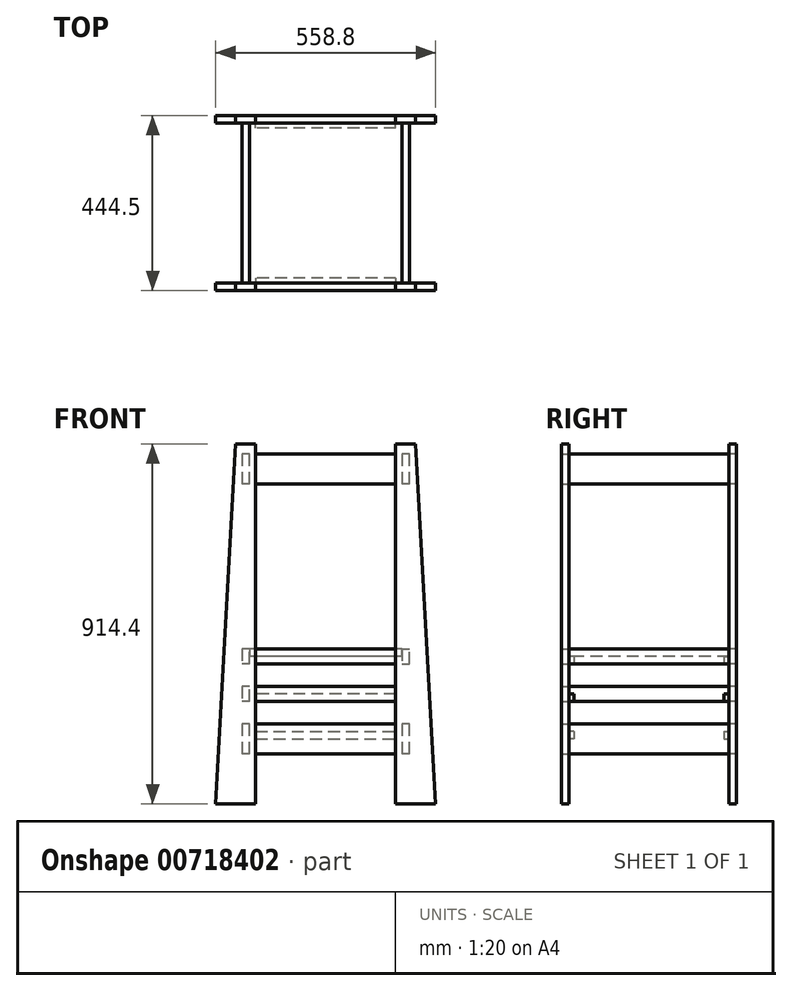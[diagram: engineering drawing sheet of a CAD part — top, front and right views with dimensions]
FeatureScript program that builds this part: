
annotation { "Feature Type Name" : "Feature", "Feature Type Description" : "" }
export const myFeature = defineFeature(function(context is Context, id is Id, definition is map)
    precondition{}
    {
        {
            var Q0;
            Q0=qCreatedBy(makeId("Front.planeOp"),FACE);
            var sketch = newSketch(context, id + "F0", { "sketchPlane" : qUnion([Q0])});
            skLineSegment(sketch, "E0", {"start": v(-279.4, 0) * mm, "end": v(-228.6, 914.4) * mm});
            skLineSegment(sketch, "E1", {"start": v(-228.6, 914.4) * mm, "end": v(-177.8, 914.4) * mm});
            skLineSegment(sketch, "E2", {"start": v(0, 494.04) * mm, "end": v(0, 0) * mm, "construction": true});
            skLineSegment(sketch, "E3", {"start": v(-279.4, 0) * mm, "end": v(-177.8, 0) * mm});
            skLineSegment(sketch, "E4", {"start": v(-177.8, 914.4) * mm, "end": v(-177.8, 0) * mm});
            skLineSegment(sketch, "E5.MirrorCS", {"start": v(228.6, 914.4) * mm, "end": v(177.8, 914.4) * mm});
            skLineSegment(sketch, "E6.MirrorCS", {"start": v(279.4, 0) * mm, "end": v(177.8, 0) * mm});
            skLineSegment(sketch, "E7.MirrorCS", {"start": v(177.8, 914.4) * mm, "end": v(177.8, 0) * mm});
            skLineSegment(sketch, "E8.bottom", {"start": v(-177.8, 889) * mm, "end": v(177.8, 889) * mm});
            skLineSegment(sketch, "E8.top", {"start": v(-177.8, 812.8) * mm, "end": v(177.8, 812.8) * mm});
            skLineSegment(sketch, "E8.left", {"start": v(-177.8, 889) * mm, "end": v(-177.8, 812.8) * mm});
            skLineSegment(sketch, "E8.right", {"start": v(177.8, 889) * mm, "end": v(177.8, 812.8) * mm});
            skLineSegment(sketch, "E9.bottom", {"start": v(-177.8, 393.7) * mm, "end": v(177.8, 393.7) * mm});
            skLineSegment(sketch, "E9.top", {"start": v(-177.8, 355.6) * mm, "end": v(177.8, 355.6) * mm});
            skLineSegment(sketch, "E9.left", {"start": v(-177.8, 393.7) * mm, "end": v(-177.8, 355.6) * mm});
            skLineSegment(sketch, "E9.right", {"start": v(177.8, 393.7) * mm, "end": v(177.8, 355.6) * mm});
            skLineSegment(sketch, "E10.bottom", {"start": v(-177.8, 298.45) * mm, "end": v(177.8, 298.45) * mm});
            skLineSegment(sketch, "E10.top", {"start": v(-177.8, 260.35) * mm, "end": v(177.8, 260.35) * mm});
            skLineSegment(sketch, "E10.left", {"start": v(-177.8, 298.45) * mm, "end": v(-177.8, 260.35) * mm});
            skLineSegment(sketch, "E10.right", {"start": v(177.8, 298.45) * mm, "end": v(177.8, 260.35) * mm});
            skLineSegment(sketch, "E11.bottom", {"start": v(-177.8, 203.2) * mm, "end": v(177.8, 203.2) * mm});
            skLineSegment(sketch, "E11.top", {"start": v(-177.8, 127) * mm, "end": v(177.8, 127) * mm});
            skLineSegment(sketch, "E11.left", {"start": v(-177.8, 203.2) * mm, "end": v(-177.8, 127) * mm});
            skLineSegment(sketch, "E11.right", {"start": v(177.8, 203.2) * mm, "end": v(177.8, 127) * mm});
            skLineSegment(sketch, "E12", {"start": v(228.6, 914.4) * mm, "end": v(279.4, 0) * mm});
            skSolve(sketch);
        }
        {
            var Q0;
            Q0=makeQuery(id+"F0.imprint","IMPRINT",FACE,{"disambiguationData":[TD([[makeQuery(id+"F0.imprint","IMPRINT",EDGE,{"derivedFrom":sQuery(id+"F0.wireOp",EDGE,"E0")}),-1.0]])]});
            var Q1;
            {var subQ6=sQuery(id+"F0.wireOp",EDGE,"E5.MirrorCS");Q1=makeQuery(id+"F0.imprint","IMPRINT",FACE,{"disambiguationData":[TD([[makeQuery(id+"F0.imprint","IMPRINT",EDGE,{"derivedFrom":subQ6}),1.0]])]});}
            extrude(context, id + "F1", {"entities" : qUnion([Q0, Q1]), "depth" : 19.05 * mm, "offsetDistance" : 25.4 * mm});
        }
        {
            var Q0;
            Q0=makeQuery(id+"F0.imprint","IMPRINT",FACE,{"disambiguationData":[TD([[makeQuery(id+"F0.imprint","IMPRINT",EDGE,{"derivedFrom":sQuery(id+"F0.wireOp",EDGE,"E8.bottom")}),-1.0]])]});
            var Q1;
            Q1=makeQuery(id+"F0.imprint","IMPRINT",FACE,{"disambiguationData":[TD([[makeQuery(id+"F0.imprint","IMPRINT",EDGE,{"derivedFrom":sQuery(id+"F0.wireOp",EDGE,"E9.bottom")}),-1.0]])]});
            var Q2;
            Q2=makeQuery(id+"F0.imprint","IMPRINT",FACE,{"disambiguationData":[TD([[makeQuery(id+"F0.imprint","IMPRINT",EDGE,{"derivedFrom":sQuery(id+"F0.wireOp",EDGE,"E10.bottom")}),-1.0]])]});
            var Q3;
            Q3=makeQuery(id+"F0.imprint","IMPRINT",FACE,{"disambiguationData":[TD([[makeQuery(id+"F0.imprint","IMPRINT",EDGE,{"derivedFrom":sQuery(id+"F0.wireOp",EDGE,"E11.bottom")}),-1.0]])]});
            extrude(context, id + "F2", {"entities" : qUnion([Q0, Q1, Q2, Q3]), "depth" : 19.05 * mm, "offsetDistance" : 25.4 * mm});
        }
        {
            var Q0;
            Q0=qCreatedBy(makeId("Front.planeOp"),FACE);
            var sketch = newSketch(context, id + "F3", { "sketchPlane" : qUnion([Q0])});
            skLineSegment(sketch, "E13.0.0", {"start": v(177.8, 374.65) * mm, "end": v(0, 374.65) * mm});
            skLineSegment(sketch, "E13.0.2", {"start": v(0, 355.6) * mm, "end": v(177.8, 355.6) * mm});
            skLineSegment(sketch, "E13.1.0", {"start": v(177.8, 279.4) * mm, "end": v(0, 279.4) * mm});
            skLineSegment(sketch, "E13.1.2", {"start": v(0, 260.35) * mm, "end": v(177.8, 260.35) * mm});
            skLineSegment(sketch, "E13.2.2", {"start": v(177.8, 184.15) * mm, "end": v(0, 184.15) * mm});
            skLineSegment(sketch, "E14", {"start": v(177.8, 374.65) * mm, "end": v(177.8, 374.65) * mm});
            skLineSegment(sketch, "E15", {"start": v(177.8, 374.65) * mm, "end": v(177.8, 355.6) * mm});
            skLineSegment(sketch, "E16", {"start": v(177.8, 355.6) * mm, "end": v(177.8, 355.6) * mm});
            skLineSegment(sketch, "E17", {"start": v(177.8, 279.4) * mm, "end": v(177.8, 279.4) * mm});
            skLineSegment(sketch, "E18", {"start": v(177.8, 279.4) * mm, "end": v(177.8, 260.35) * mm});
            skLineSegment(sketch, "E19", {"start": v(177.8, 260.35) * mm, "end": v(177.8, 260.35) * mm});
            skLineSegment(sketch, "E20", {"start": v(177.8, 184.15) * mm, "end": v(177.8, 184.15) * mm});
            skLineSegment(sketch, "E21", {"start": v(177.8, 184.15) * mm, "end": v(177.8, 165.1) * mm});
            skLineSegment(sketch, "E22.0", {"start": v(0, 494.04) * mm, "end": v(0, 0) * mm, "construction": true});
            skPoint(sketch, "E13.0.1.end.orphan", {"position": v(-177.8, 355.6) * mm});
            skPoint(sketch, "E13.0.1.start.orphan", {"position": v(-177.8, 393.7) * mm});
            skPoint(sketch, "E23.orphan", {"position": v(-177.8, 260.35) * mm});
            skPoint(sketch, "E13.2.3.start.orphan", {"position": v(-177.8, 184.15) * mm});
            skLineSegment(sketch, "E24", {"start": v(177.8, 165.1) * mm, "end": v(0, 165.1) * mm});
            skLineSegment(sketch, "E25.MirrorCS", {"start": v(-177.8, 184.15) * mm, "end": v(-177.8, 165.1) * mm});
            skLineSegment(sketch, "E26.MirrorCS", {"start": v(-177.8, 279.4) * mm, "end": v(-177.8, 260.35) * mm});
            skLineSegment(sketch, "E27.MirrorCS", {"start": v(-177.8, 374.65) * mm, "end": v(-177.8, 355.6) * mm});
            skLineSegment(sketch, "E28.MirrorCS", {"start": v(0, 355.6) * mm, "end": v(-177.8, 355.6) * mm});
            skLineSegment(sketch, "E29.MirrorCS", {"start": v(-177.8, 374.65) * mm, "end": v(-177.8, 374.65) * mm});
            skLineSegment(sketch, "E30.MirrorCS", {"start": v(-177.8, 184.15) * mm, "end": v(0, 184.15) * mm});
            skLineSegment(sketch, "E31.MirrorCS", {"start": v(-177.8, 374.65) * mm, "end": v(0, 374.65) * mm});
            skLineSegment(sketch, "E32.MirrorCS", {"start": v(-177.8, 184.15) * mm, "end": v(-177.8, 184.15) * mm});
            skLineSegment(sketch, "E33.MirrorCS", {"start": v(-177.8, 355.6) * mm, "end": v(-177.8, 355.6) * mm});
            skLineSegment(sketch, "E34.MirrorCS", {"start": v(-177.8, 279.4) * mm, "end": v(0, 279.4) * mm});
            skLineSegment(sketch, "E35.MirrorCS", {"start": v(-177.8, 165.1) * mm, "end": v(0, 165.1) * mm});
            skLineSegment(sketch, "E36.MirrorCS", {"start": v(-177.8, 260.35) * mm, "end": v(-177.8, 260.35) * mm});
            skLineSegment(sketch, "E37.MirrorCS", {"start": v(0, 260.35) * mm, "end": v(-177.8, 260.35) * mm});
            skLineSegment(sketch, "E38.MirrorCS", {"start": v(-177.8, 279.4) * mm, "end": v(-177.8, 279.4) * mm});
            skSolve(sketch);
        }
        {
            var Q0;
            Q0 = qSketchRegion(id + "F3", true);
            extrude(context, id + "F4", {"entities" : qUnion([Q0]), "oppositeDirection" : true, "depth" : 12.7 * mm, "offsetDistance" : 25.4 * mm});
        }
        {
            var Q0;
            Q0=qCreatedBy(makeId("Front.planeOp"),FACE);
            cPlane(context, id + "F5", {"entities" : qUnion([Q0]), "cplaneType" : CPlaneType.OFFSET, "offset" : 203.2 * mm, "oppositeDirection" : true, "width" : 152.4 * mm, "height" : 152.4 * mm});
        }
        {
            var Q0;
            Q0=makeQuery(id+"F2.opExtrude","SWEPT_BODY",BODY,{"disambiguationData":[OSD([sQuery(id+"F0.wireOp",EDGE,"E8.bottom"),sQuery(id+"F0.wireOp",EDGE,"E8.left"),sQuery(id+"F0.wireOp",EDGE,"E8.right"),sQuery(id+"F0.wireOp",EDGE,"LwXmSMC4-AZGY-xB09-EJig-U2rCeK0o0KCN")])]});
            var Q1;
            Q1=makeQuery(id+"F2.opExtrude","SWEPT_BODY",BODY,{"disambiguationData":[OSD([sQuery(id+"F0.wireOp",EDGE,"E10.bottom"),sQuery(id+"F0.wireOp",EDGE,"E10.top"),sQuery(id+"F0.wireOp",EDGE,"E10.left"),sQuery(id+"F0.wireOp",EDGE,"E10.right")])]});
            var Q2;
            Q2=makeQuery(id+"F2.opExtrude","SWEPT_BODY",BODY,{"disambiguationData":[OSD([sQuery(id+"F0.wireOp",EDGE,"E11.bottom"),sQuery(id+"F0.wireOp",EDGE,"E11.left"),sQuery(id+"F0.wireOp",EDGE,"E11.right"),sQuery(id+"F0.wireOp",EDGE,"WeQ5YnD7-XFgI-7NGZ-9cHd-fthih7jxop2D")])]});
            var Q3;
            Q3=makeQuery(id+"F4.opExtrude","SWEPT_BODY",BODY,{"disambiguationData":[OSD([sQuery(id+"F3.wireOp",EDGE,"E13.0.0"),sQuery(id+"F3.wireOp",EDGE,"E13.0.2"),sQuery(id+"F3.wireOp",EDGE,"E14"),sQuery(id+"F3.wireOp",EDGE,"E15"),sQuery(id+"F3.wireOp",EDGE,"E16"),sQuery(id+"F3.wireOp",EDGE,"E27.MirrorCS"),sQuery(id+"F3.wireOp",EDGE,"E28.MirrorCS"),sQuery(id+"F3.wireOp",EDGE,"E29.MirrorCS"),sQuery(id+"F3.wireOp",EDGE,"E31.MirrorCS"),sQuery(id+"F3.wireOp",EDGE,"E33.MirrorCS")])]});
            var Q4;
            Q4=makeQuery(id+"F2.opExtrude","SWEPT_BODY",BODY,{"disambiguationData":[OSD([sQuery(id+"F0.wireOp",EDGE,"E9.bottom"),sQuery(id+"F0.wireOp",EDGE,"E9.top"),sQuery(id+"F0.wireOp",EDGE,"E9.left"),sQuery(id+"F0.wireOp",EDGE,"E9.right")])]});
            var Q5;
            Q5=makeQuery(id+"F1.opExtrude","SWEPT_BODY",BODY,{"disambiguationData":[OSD([sQuery(id+"F0.wireOp",EDGE,"E5.MirrorCS"),sQuery(id+"F0.wireOp",EDGE,"E6.MirrorCS"),sQuery(id+"F0.wireOp",EDGE,"021805e8-8c5c-4a1d-8333-e249b14e6f0c2.MirrorCS"),sQuery(id+"F0.wireOp",EDGE,"E7.MirrorCS"),sQuery(id+"F0.wireOp",EDGE,"E8.right"),sQuery(id+"F0.wireOp",EDGE,"E9.right"),sQuery(id+"F0.wireOp",EDGE,"E10.right"),sQuery(id+"F0.wireOp",EDGE,"E11.right")])]});
            var Q6;
            Q6=makeQuery(id+"F1.opExtrude","SWEPT_BODY",BODY,{"disambiguationData":[OSD([sQuery(id+"F0.wireOp",EDGE,"E0"),sQuery(id+"F0.wireOp",EDGE,"E1"),sQuery(id+"F0.wireOp",EDGE,"E3"),sQuery(id+"F0.wireOp",EDGE,"E4"),sQuery(id+"F0.wireOp",EDGE,"E8.left"),sQuery(id+"F0.wireOp",EDGE,"E9.left"),sQuery(id+"F0.wireOp",EDGE,"E10.left"),sQuery(id+"F0.wireOp",EDGE,"E11.left")])]});
            var Q7;
            Q7=makeQuery(id+"F4.opExtrude","SWEPT_BODY",BODY,{"disambiguationData":[OSD([sQuery(id+"F3.wireOp",EDGE,"E13.2.2"),sQuery(id+"F3.wireOp",EDGE,"E20"),sQuery(id+"F3.wireOp",EDGE,"E21"),sQuery(id+"F3.wireOp",EDGE,"E24"),sQuery(id+"F3.wireOp",EDGE,"E25.MirrorCS"),sQuery(id+"F3.wireOp",EDGE,"E30.MirrorCS"),sQuery(id+"F3.wireOp",EDGE,"E32.MirrorCS"),sQuery(id+"F3.wireOp",EDGE,"E35.MirrorCS")])]});
            var Q8;
            Q8=makeQuery(id+"F4.opExtrude","SWEPT_BODY",BODY,{"disambiguationData":[OSD([sQuery(id+"F3.wireOp",EDGE,"E13.1.0"),sQuery(id+"F3.wireOp",EDGE,"E13.1.2"),sQuery(id+"F3.wireOp",EDGE,"E17"),sQuery(id+"F3.wireOp",EDGE,"E18"),sQuery(id+"F3.wireOp",EDGE,"E19"),sQuery(id+"F3.wireOp",EDGE,"E26.MirrorCS"),sQuery(id+"F3.wireOp",EDGE,"E34.MirrorCS"),sQuery(id+"F3.wireOp",EDGE,"E36.MirrorCS"),sQuery(id+"F3.wireOp",EDGE,"E37.MirrorCS"),sQuery(id+"F3.wireOp",EDGE,"E38.MirrorCS")])]});
            var Q9;
            Q9=qCreatedBy(id+"F5.planeOp",FACE);
            mirror(context, id + "F6", {"entities" : qUnion([Q0, Q1, Q2, Q3, Q4, Q5, Q6, Q7, Q8]), "mirrorPlane" : qUnion([Q9])});
        }
        {
            var Q0;
            Q0=qCreatedBy(id+"F5.planeOp",FACE);
            var sketch = newSketch(context, id + "F7", { "sketchPlane" : qUnion([Q0])});
            skLineSegment(sketch, "E39.bottom", {"start": v(-212.73, 203.2) * mm, "end": v(-193.68, 203.2) * mm});
            skLineSegment(sketch, "E39.top", {"start": v(-212.73, 127) * mm, "end": v(-193.68, 127) * mm});
            skLineSegment(sketch, "E39.left", {"start": v(-212.73, 203.2) * mm, "end": v(-212.73, 127) * mm});
            skLineSegment(sketch, "E39.right", {"start": v(-193.68, 203.2) * mm, "end": v(-193.68, 127) * mm});
            skLineSegment(sketch, "E40.bottom", {"start": v(-212.73, 889) * mm, "end": v(-193.67, 889) * mm});
            skLineSegment(sketch, "E40.top", {"start": v(-212.73, 812.8) * mm, "end": v(-193.67, 812.8) * mm});
            skLineSegment(sketch, "E40.left", {"start": v(-212.72, 889) * mm, "end": v(-212.72, 812.8) * mm});
            skLineSegment(sketch, "E40.right", {"start": v(-193.67, 889) * mm, "end": v(-193.67, 812.8) * mm});
            skLineSegment(sketch, "E41", {"start": v(-203.2, 914.4) * mm, "end": v(-203.2, 0) * mm, "construction": true});
            skPoint(sketch, "E42", {"position": v(-203.2, 203.2) * mm});
            skLineSegment(sketch, "E43.bottom", {"start": v(193.68, 889) * mm, "end": v(212.73, 889) * mm});
            skLineSegment(sketch, "E43.top", {"start": v(193.68, 812.8) * mm, "end": v(212.73, 812.8) * mm});
            skLineSegment(sketch, "E43.left", {"start": v(193.68, 889) * mm, "end": v(193.68, 812.8) * mm});
            skLineSegment(sketch, "E43.right", {"start": v(212.73, 889) * mm, "end": v(212.73, 812.8) * mm});
            skLineSegment(sketch, "E44", {"start": v(203.2, 889) * mm, "end": v(203.2, 812.8) * mm, "construction": true});
            skLineSegment(sketch, "E45", {"start": v(-212.72, 889) * mm, "end": v(-193.68, 812.8) * mm, "construction": true});
            skPoint(sketch, "E46", {"position": v(-203.2, 850.9) * mm});
            skLineSegment(sketch, "E47.bottom", {"start": v(193.68, 203.2) * mm, "end": v(212.73, 203.2) * mm});
            skLineSegment(sketch, "E47.top", {"start": v(193.68, 127) * mm, "end": v(212.73, 127) * mm});
            skLineSegment(sketch, "E47.left", {"start": v(193.68, 203.2) * mm, "end": v(193.68, 127) * mm});
            skLineSegment(sketch, "E47.right", {"start": v(212.72, 203.2) * mm, "end": v(212.72, 127) * mm});
            skLineSegment(sketch, "E48.bottom", {"start": v(-212.73, 298.45) * mm, "end": v(-193.67, 298.45) * mm});
            skLineSegment(sketch, "E48.top", {"start": v(-212.73, 260.35) * mm, "end": v(-193.67, 260.35) * mm});
            skLineSegment(sketch, "E48.left", {"start": v(-212.73, 298.45) * mm, "end": v(-212.73, 260.35) * mm});
            skLineSegment(sketch, "E48.right", {"start": v(-193.67, 298.45) * mm, "end": v(-193.67, 260.35) * mm});
            skPoint(sketch, "E48.middle", {"position": v(-203.2, 279.4) * mm});
            skLineSegment(sketch, "E49.bottom", {"start": v(-212.73, 393.7) * mm, "end": v(-193.68, 393.7) * mm});
            skLineSegment(sketch, "E49.top", {"start": v(-212.73, 355.6) * mm, "end": v(-193.68, 355.6) * mm});
            skLineSegment(sketch, "E49.left", {"start": v(-212.73, 393.7) * mm, "end": v(-212.73, 355.6) * mm});
            skLineSegment(sketch, "E49.right", {"start": v(-193.68, 393.7) * mm, "end": v(-193.68, 355.6) * mm});
            skPoint(sketch, "E49.middle", {"position": v(-203.2, 374.65) * mm});
            skLineSegment(sketch, "E50.MirrorCS", {"start": v(193.68, 393.7) * mm, "end": v(193.68, 355.6) * mm});
            skLineSegment(sketch, "E51.MirrorCS", {"start": v(212.73, 393.7) * mm, "end": v(193.68, 393.7) * mm});
            skLineSegment(sketch, "E52.MirrorCS", {"start": v(212.73, 298.45) * mm, "end": v(193.67, 298.45) * mm});
            skLineSegment(sketch, "E53.MirrorCS", {"start": v(212.73, 355.6) * mm, "end": v(193.68, 355.6) * mm});
            skLineSegment(sketch, "E54.MirrorCS", {"start": v(212.73, 260.35) * mm, "end": v(193.67, 260.35) * mm});
            skPoint(sketch, "E55.MirrorP", {"position": v(203.2, 279.4) * mm});
            skLineSegment(sketch, "E56.MirrorCS", {"start": v(193.67, 298.45) * mm, "end": v(193.67, 260.35) * mm});
            skLineSegment(sketch, "E57.MirrorCS", {"start": v(212.73, 298.45) * mm, "end": v(212.73, 260.35) * mm});
            skLineSegment(sketch, "E58.MirrorCS", {"start": v(212.73, 393.7) * mm, "end": v(212.73, 355.6) * mm});
            skPoint(sketch, "E59.MirrorP", {"position": v(203.2, 374.65) * mm});
            skLineSegment(sketch, "E60", {"start": v(0, 889) * mm, "end": v(0, 127) * mm, "construction": true});
            skSolve(sketch);
        }
        {
            var Q0;
            Q0=makeQuery(id+"F7.imprint","IMPRINT",FACE,{"disambiguationData":[TD([[makeQuery(id+"F7.imprint","IMPRINT",EDGE,{"derivedFrom":sQuery(id+"F7.wireOp",EDGE,"E43.bottom")}),-1.0]])]});
            var Q1;
            Q1=makeQuery(id+"F7.imprint","IMPRINT",FACE,{"disambiguationData":[TD([[makeQuery(id+"F7.imprint","IMPRINT",EDGE,{"derivedFrom":sQuery(id+"F7.wireOp",EDGE,"E40.bottom")}),-1.0]])]});
            var Q2;
            Q2=makeQuery(id+"F7.imprint","IMPRINT",FACE,{"disambiguationData":[TD([[makeQuery(id+"F7.imprint","IMPRINT",EDGE,{"derivedFrom":sQuery(id+"F7.wireOp",EDGE,"E49.bottom")}),-1.0]])]});
            var Q3;
            Q3=makeQuery(id+"F7.imprint","IMPRINT",FACE,{"disambiguationData":[TD([[makeQuery(id+"F7.imprint","IMPRINT",EDGE,{"derivedFrom":sQuery(id+"F7.wireOp",EDGE,"E48.bottom")}),-1.0]])]});
            var Q4;
            Q4=makeQuery(id+"F7.imprint","IMPRINT",FACE,{"disambiguationData":[TD([[makeQuery(id+"F7.imprint","IMPRINT",EDGE,{"derivedFrom":sQuery(id+"F7.wireOp",EDGE,"E39.bottom")}),-1.0]])]});
            var Q5;
            Q5=makeQuery(id+"F7.imprint","IMPRINT",FACE,{"disambiguationData":[TD([[makeQuery(id+"F7.imprint","IMPRINT",EDGE,{"derivedFrom":sQuery(id+"F7.wireOp",EDGE,"E47.bottom")}),-1.0]])]});
            var Q6;
            Q6=makeQuery(id+"F7.imprint","IMPRINT",FACE,{"disambiguationData":[TD([[makeQuery(id+"F7.imprint","IMPRINT",EDGE,{"derivedFrom":sQuery(id+"F7.wireOp",EDGE,"E50.MirrorCS")}),1.0]])]});
            var Q7;
            Q7=makeQuery(id+"F6.opPattern","COPY",FACE,{"derivedFrom":makeQuery(id+"F1.opExtrude","CAP_FACE",FACE,{"disambiguationData":[OSD([sQuery(id+"F0.wireOp",EDGE,"E0"),sQuery(id+"F0.wireOp",EDGE,"E1"),sQuery(id+"F0.wireOp",EDGE,"E3"),sQuery(id+"F0.wireOp",EDGE,"E4"),sQuery(id+"F0.wireOp",EDGE,"E8.left"),sQuery(id+"F0.wireOp",EDGE,"E9.left"),sQuery(id+"F0.wireOp",EDGE,"E10.left"),sQuery(id+"F0.wireOp",EDGE,"E11.left")])],"isStart":true}),"instanceName":"1"});
            var Q8;
            Q8=makeQuery(id+"F1.opExtrude","CAP_FACE",FACE,{"disambiguationData":[OSD([sQuery(id+"F0.wireOp",EDGE,"E0"),sQuery(id+"F0.wireOp",EDGE,"E1"),sQuery(id+"F0.wireOp",EDGE,"E3"),sQuery(id+"F0.wireOp",EDGE,"E4"),sQuery(id+"F0.wireOp",EDGE,"E8.left"),sQuery(id+"F0.wireOp",EDGE,"E9.left"),sQuery(id+"F0.wireOp",EDGE,"E10.left"),sQuery(id+"F0.wireOp",EDGE,"E11.left")])],"isStart":true});
            extrude(context, id + "F8", {"entities" : qUnion([Q0, Q1, Q2, Q3, Q4, Q5, Q6]), "endBound" : BoundingType.UP_TO_SURFACE, "oppositeDirection" : true, "depth" : 25.4 * mm, "endBoundEntityFace" : qUnion([Q7]), "offsetDistance" : 25.4 * mm, "hasSecondDirection" : true, "secondDirectionBound" : SecondDirectionBoundingType.UP_TO_SURFACE, "secondDirectionOppositeDirection" : false, "secondDirectionDepth" : 25.4 * mm, "secondDirectionBoundEntityFace" : qUnion([Q8])});
        }
        {
            var Q0;
            Q0=qCreatedBy(id+"F5.planeOp",FACE);
            var sketch = newSketch(context, id + "F9", { "sketchPlane" : qUnion([Q0])});
            skLineSegment(sketch, "E61.bottom", {"start": v(-193.68, 393.7) * mm, "end": v(193.68, 393.7) * mm});
            skLineSegment(sketch, "E61.top", {"start": v(-193.68, 374.65) * mm, "end": v(193.68, 374.65) * mm});
            skLineSegment(sketch, "E62.right", {"start": v(-193.68, 393.7) * mm, "end": v(-193.68, 374.65) * mm});
            skLineSegment(sketch, "E63.left", {"start": v(193.68, 393.7) * mm, "end": v(193.68, 374.65) * mm});
            skSolve(sketch);
        }
        {
            var Q0;
            Q0 = qSketchRegion(id + "F9", true);
            var Q1;
            Q1=makeQuery(id+"F6.opPattern","COPY",FACE,{"derivedFrom":makeQuery(id+"F1.opExtrude","CAP_FACE",FACE,{"disambiguationData":[OSD([sQuery(id+"F0.wireOp",EDGE,"E0"),sQuery(id+"F0.wireOp",EDGE,"E1"),sQuery(id+"F0.wireOp",EDGE,"E3"),sQuery(id+"F0.wireOp",EDGE,"E4"),sQuery(id+"F0.wireOp",EDGE,"E8.left"),sQuery(id+"F0.wireOp",EDGE,"E9.left"),sQuery(id+"F0.wireOp",EDGE,"E10.left"),sQuery(id+"F0.wireOp",EDGE,"E11.left")])],"isStart":true}),"instanceName":"1"});
            var Q2;
            Q2=makeQuery(id+"F1.opExtrude","CAP_FACE",FACE,{"disambiguationData":[OSD([sQuery(id+"F0.wireOp",EDGE,"E0"),sQuery(id+"F0.wireOp",EDGE,"E1"),sQuery(id+"F0.wireOp",EDGE,"E3"),sQuery(id+"F0.wireOp",EDGE,"E4"),sQuery(id+"F0.wireOp",EDGE,"E8.left"),sQuery(id+"F0.wireOp",EDGE,"E9.left"),sQuery(id+"F0.wireOp",EDGE,"E10.left"),sQuery(id+"F0.wireOp",EDGE,"E11.left")])],"isStart":true});
            extrude(context, id + "F10", {"entities" : qUnion([Q0]), "endBound" : BoundingType.UP_TO_SURFACE, "oppositeDirection" : true, "depth" : 25.4 * mm, "endBoundEntityFace" : qUnion([Q1]), "offsetDistance" : 25.4 * mm, "hasSecondDirection" : true, "secondDirectionBound" : SecondDirectionBoundingType.UP_TO_SURFACE, "secondDirectionOppositeDirection" : false, "secondDirectionDepth" : 25.4 * mm, "secondDirectionBoundEntityFace" : qUnion([Q2])});
        }
    });
